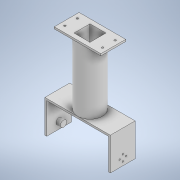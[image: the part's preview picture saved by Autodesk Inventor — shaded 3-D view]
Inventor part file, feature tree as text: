
AUTODESK INVENTOR PART (.ipt)
format: ipt  version: 2022 (Build 260153000, 153)  size: 250,368 bytes
history: native  units: mm
features: extrude x14, sketch x14
ambient origin geometry x8: Origin, YZ Plane, XZ Plane, XY Plane, X Axis, Y Axis, Z Axis, Center Point
bodies: Solid1 (feature_tree)
feature tree (28):
  extrude  "Extrusion1"  Depth=98.0mm
  extrude  "Extrusion2"  Depth=3.0mm
  extrude  "Extrusion3"  Depth=25.4mm TaperAngle=0.0deg
  extrude  "Extrusion4"  Depth=40.0mm TaperAngle=360.0deg
  extrude  "Extrusion5"  Depth=1.0mm TaperAngle=0.0deg
  extrude  "Extrusion6"  Depth=16.0mm
  extrude  "Extrusion7"  Depth=10.0mm
  extrude  "Extrusion8"  Depth=7.0mm TaperAngle=0.0deg
  extrude  "Extrusion9"  Depth=101.6mm TaperAngle=0.0deg
  extrude  "Extrusion10"  Depth=25.4mm
  extrude  "Extrusion16"  Depth=3.0mm TaperAngle=0.0deg
  extrude  "Extrusion17"  Depth=15.0mm TaperAngle=0.0deg
  extrude  "Extrusion18"  Depth=15.0mm
  extrude  "Extrusion19"  [1 undecoded]
  sketch  "Sketch1"  dims[d0=45.0mm d1=98.0mm]
  sketch  "Sketch2"  dims[d2=3.0mm d3=48.0mm]
  sketch  "Sketch3"  dims[d4=104.0mm d5=25.4mm d6=0.0mm]
  sketch  "Sketch4"  dims[d10=2.25mm d11=40.0mm d13=360.0deg]
  sketch  "Sketch5"  dims[d15=25.4mm d16=0.0mm d17=1.0mm d18=0.0mm]
  sketch  "Sketch6"  dims[d19=4.0mm d20=0.0mm d21=16.0mm]
  sketch  "Sketch8"  dims[d22=1.0mm d23=0.0mm d26=10.0mm]
  sketch  "Sketch9"  dims[d27=7.0mm d28=0.0mm d37=7.0mm d38=0.0mm]
  sketch  "Sketch10"  dims[d39=7.0mm d40=0.0mm d41=101.6mm d42=0.0mm]
  sketch  "Sketch11"  dims[d45=25.4mm d46=25.4mm]
  sketch  "Sketch12"  dims[d47=101.6mm d48=0.0mm d71=3.0mm d72=0.0mm]
  sketch  "Sketch17"  dims[d79=0.0mm d80=0.0mm d81=15.0mm d82=0.0mm]
  sketch  "Sketch18"  dims[d83=15.0mm d84=0.0mm d49=0.5mm]
  sketch  "Sketch19"  dims[d50=0.872665mm]
note: 1 required parameter value undecoded (feature->parameter linkage not recoverable at this tier; creation-order binding heuristic only, values carry confidence <= 0.55)
